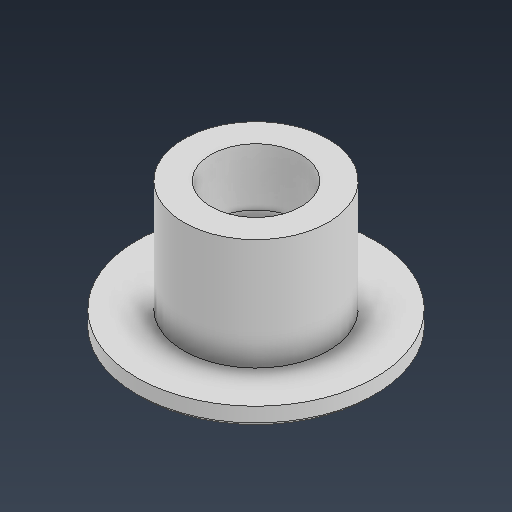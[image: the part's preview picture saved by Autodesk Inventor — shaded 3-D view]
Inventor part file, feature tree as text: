
AUTODESK INVENTOR PART (.ipt)
format: ipt  version: 2021 (Build 250183000, 183)  size: 115,200 bytes
history: native  units: in
note: dims shown in document units (in); Inventor stores cm internally (conversion verified against a paired STEP export)
features: chamfer x1
ambient origin geometry x8: Origin, YZ Plane, XZ Plane, XY Plane, X Axis, Y Axis, Z Axis, Center Point
bodies: Solid1 (feature_tree)
feature tree (1):
  chamfer  "Chamfer1"  [1 undecoded]
note: 1 required parameter value undecoded (feature->parameter linkage not recoverable at this tier; creation-order binding heuristic only, values carry confidence <= 0.55)
